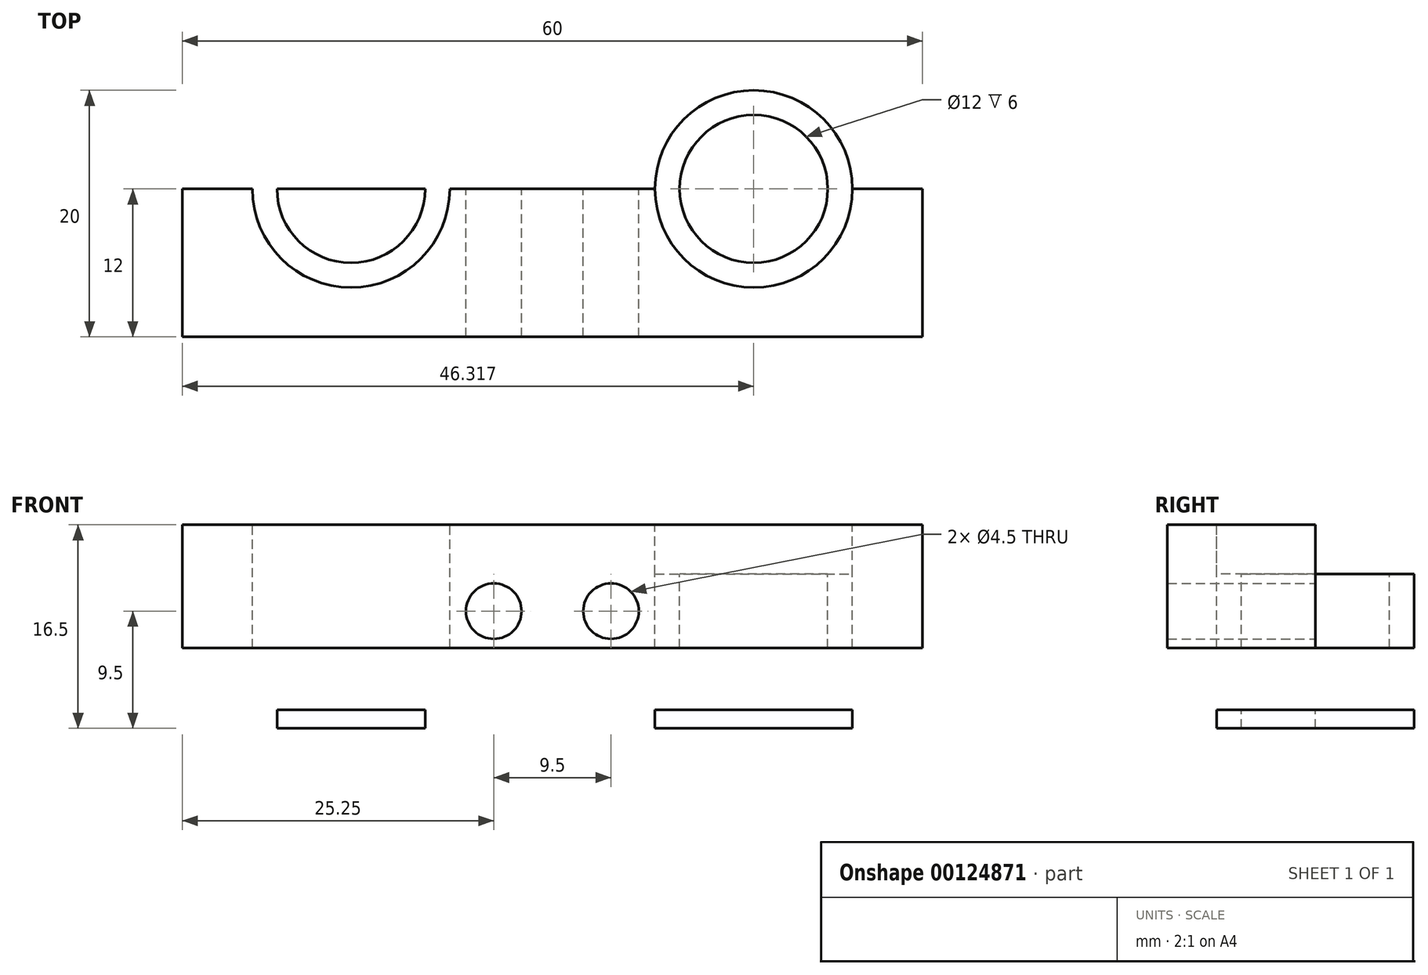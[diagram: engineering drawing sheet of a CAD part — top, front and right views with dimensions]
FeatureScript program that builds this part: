
annotation { "Feature Type Name" : "Feature", "Feature Type Description" : "" }
export const myFeature = defineFeature(function(context is Context, id is Id, definition is map)
    precondition{}
    {
        {
            var Q0;
            Q0=qCreatedBy(makeId("Top.planeOp"),FACE);
            var sketch = newSketch(context, id + "F0", { "sketchPlane" : qUnion([Q0])});
            skLineSegment(sketch, "E0.bottom", {"start": v(43, -44.5) * mm, "end": v(-43, -44.5) * mm});
            skLineSegment(sketch, "E0.top", {"start": v(43, 44.5) * mm, "end": v(-43, 44.5) * mm});
            skLineSegment(sketch, "E0.left", {"start": v(43, -44.5) * mm, "end": v(43, 44.5) * mm});
            skLineSegment(sketch, "E0.right", {"start": v(-43, -44.5) * mm, "end": v(-43, 44.5) * mm});
            skPoint(sketch, "E0.middle", {"position": v(0, 0) * mm});
            skLineSegment(sketch, "E1.bottom", {"start": v(-31, 25.5) * mm, "end": v(31, 25.5) * mm});
            skLineSegment(sketch, "E1.top", {"start": v(-31, -11.5) * mm, "end": v(31, -11.5) * mm});
            skLineSegment(sketch, "E1.left", {"start": v(-31, 25.5) * mm, "end": v(-31, -11.5) * mm});
            skLineSegment(sketch, "E1.right", {"start": v(31, 25.5) * mm, "end": v(31, -11.5) * mm});
            skLineSegment(sketch, "E2.bottom", {"start": v(43, 13.5) * mm, "end": v(31, 13.5) * mm});
            skLineSegment(sketch, "E2.top", {"start": v(43, -3) * mm, "end": v(31, -3) * mm});
            skLineSegment(sketch, "E2.left", {"start": v(43, 13.5) * mm, "end": v(43, -3) * mm});
            skLineSegment(sketch, "E2.right", {"start": v(-43, 13.5) * mm, "end": v(-43, -3) * mm});
            skLineSegment(sketch, "E3", {"start": v(-43, 5.25) * mm, "end": v(-31, 5.25) * mm, "construction": true});
            skLineSegment(sketch, "E4.trimOffspring", {"start": v(-31, 13.5) * mm, "end": v(-43, 13.5) * mm});
            skLineSegment(sketch, "E5.trimOffspring", {"start": v(-31, -3) * mm, "end": v(-43, -3) * mm});
            skLineSegment(sketch, "E6.trimOffspring", {"start": v(31, 5.25) * mm, "end": v(43, 5.25) * mm, "construction": true});
            skPoint(sketch, "E7", {"position": v(-37, 5.25) * mm});
            skPoint(sketch, "E8", {"position": v(37, 5.25) * mm});
            skCircle(sketch, "E9", {"center": v(37, 5.25) * mm, "radius": 1.6 * mm});
            skPoint(sketch, "E10", {"position": v(38.6, 5.25) * mm});
            skCircle(sketch, "E11.MirrorC", {"center": v(-37, 5.25) * mm, "radius": 1.6 * mm});
            skSolve(sketch);
        }
        {
            var Q0;
            Q0=qSketchRegion(id+"F0",true);
            extrude(context, id + "F1", {"entities" : qUnion([Q0]), "depth" : 17.5 * mm});
        }
        {
            var Q0;
            Q0=makeQuery(id+"F1.opExtrude","CAP_FACE",FACE,{"disambiguationData":[OSD([sQuery(id+"F0.wireOp",EDGE,"E0.bottom"),sQuery(id+"F0.wireOp",EDGE,"E0.top"),sQuery(id+"F0.wireOp",EDGE,"E0.left"),sQuery(id+"F0.wireOp",EDGE,"E0.right"),sQuery(id+"F0.wireOp",EDGE,"E1.bottom"),sQuery(id+"F0.wireOp",EDGE,"E1.top"),sQuery(id+"F0.wireOp",EDGE,"E1.left"),sQuery(id+"F0.wireOp",EDGE,"E1.right"),sQuery(id+"F0.wireOp",EDGE,"E2.left"),sQuery(id+"F0.wireOp",EDGE,"E2.right"),sQuery(id+"F0.wireOp",EDGE,"E9"),sQuery(id+"F0.wireOp",EDGE,"E11.MirrorC")])],"isStart":false});
            var sketch = newSketch(context, id + "F2", { "sketchPlane" : qUnion([Q0])});
            skLineSegment(sketch, "E12.bottom", {"start": v(43, -2.95) * mm, "end": v(31, -2.95) * mm});
            skLineSegment(sketch, "E12.top", {"start": v(43, 13.45) * mm, "end": v(31, 13.45) * mm});
            skLineSegment(sketch, "E12.left", {"start": v(43, -2.95) * mm, "end": v(43, 13.45) * mm});
            skLineSegment(sketch, "E12.right", {"start": v(-43, -2.95) * mm, "end": v(-43, 13.45) * mm});
            skPoint(sketch, "E13", {"position": v(37, 5.25) * mm});
            skLineSegment(sketch, "E14", {"start": v(43, 5.25) * mm, "end": v(31, 5.25) * mm, "construction": true});
            skLineSegment(sketch, "E15.0", {"start": v(31, 25.5) * mm, "end": v(31, -11.5) * mm});
            skLineSegment(sketch, "E15.1", {"start": v(-31, 25.5) * mm, "end": v(-31, -11.5) * mm});
            skLineSegment(sketch, "E16.trimOffspring", {"start": v(-31, -2.95) * mm, "end": v(-43, -2.95) * mm});
            skLineSegment(sketch, "E17.trimOffspring", {"start": v(-31, 13.45) * mm, "end": v(-43, 13.45) * mm});
            skLineSegment(sketch, "E18.trimOffspring", {"start": v(-31, 5.25) * mm, "end": v(-43, 5.25) * mm, "construction": true});
            skSolve(sketch);
        }
        {
            var Q0;
            Q0=qCreatedBy(makeId("Top.planeOp"),FACE);
            var sketch = newSketch(context, id + "F3", { "sketchPlane" : qUnion([Q0])});
            skCircle(sketch, "E19", {"center": v(16.32, 5.25) * mm, "radius": 11.2 * mm});
            skCircle(sketch, "E20.0", {"center": v(-37, 5.25) * mm, "radius": 1.6 * mm});
            skLineSegment(sketch, "E21", {"start": v(-37, 5.25) * mm, "end": v(47.23, 5.25) * mm, "construction": true});
            skCircle(sketch, "E22.MirrorC", {"center": v(-16.32, 5.25) * mm, "radius": 11.2 * mm});
            skSolve(sketch);
        }
        {
            var Q0;
            Q0=makeQuery(id+"F3.imprint","IMPRINT",FACE,{"disambiguationData":[TD([[makeQuery(id+"F3.imprint","IMPRINT",EDGE,{"derivedFrom":sQuery(id+"F3.wireOp",EDGE,"E19")}),1.0]])]});
            var Q1;
            Q1=makeQuery(id+"F3.imprint","IMPRINT",FACE,{"disambiguationData":[TD([[makeQuery(id+"F3.imprint","IMPRINT",EDGE,{"derivedFrom":sQuery(id+"F3.wireOp",EDGE,"E22.MirrorC")}),-1.0]])]});
            extrude(context, id + "F4", {"entities" : qUnion([Q0, Q1]), "depth" : (26 + 14.5) * mm, "hasSecondDirection" : true, "secondDirectionOppositeDirection" : false, "secondDirectionDepth" : 14.5 * mm});
        }
        {
            var Q0;
            Q0=makeQuery(id+"F1.opExtrude","CAP_FACE",FACE,{"disambiguationData":[OSD([sQuery(id+"F0.wireOp",EDGE,"E0.bottom"),sQuery(id+"F0.wireOp",EDGE,"E0.top"),sQuery(id+"F0.wireOp",EDGE,"E0.left"),sQuery(id+"F0.wireOp",EDGE,"E0.right"),sQuery(id+"F0.wireOp",EDGE,"E1.bottom"),sQuery(id+"F0.wireOp",EDGE,"E1.top"),sQuery(id+"F0.wireOp",EDGE,"E1.left"),sQuery(id+"F0.wireOp",EDGE,"E1.right"),sQuery(id+"F0.wireOp",EDGE,"E2.left"),sQuery(id+"F0.wireOp",EDGE,"E2.right"),sQuery(id+"F0.wireOp",EDGE,"E9"),sQuery(id+"F0.wireOp",EDGE,"E11.MirrorC")])],"isStart":false});
            var sketch = newSketch(context, id + "F5", { "sketchPlane" : qUnion([Q0])});
            skLineSegment(sketch, "E23.bottom", {"start": v(-43, 13.5) * mm, "end": v(-31, 13.5) * mm});
            skLineSegment(sketch, "E23.top", {"start": v(-43, -3) * mm, "end": v(-31, -3) * mm});
            skLineSegment(sketch, "E23.left", {"start": v(-43, 13.5) * mm, "end": v(-43, -3) * mm});
            skLineSegment(sketch, "E23.right", {"start": v(43, 13.5) * mm, "end": v(43, -3) * mm});
            skPoint(sketch, "E24", {"position": v(43, 5.25) * mm});
            skPoint(sketch, "E25", {"position": v(-43, 5.25) * mm});
            skLineSegment(sketch, "E26", {"start": v(-31, 13.5) * mm, "end": v(-31, -3) * mm});
            skLineSegment(sketch, "E27", {"start": v(31, 13.5) * mm, "end": v(31, -3) * mm});
            skLineSegment(sketch, "E28.trimOffspring", {"start": v(31, 13.5) * mm, "end": v(43, 13.5) * mm});
            skLineSegment(sketch, "E29.trimOffspring", {"start": v(31, -3) * mm, "end": v(43, -3) * mm});
            skSolve(sketch);
        }
        {
            var Q0;
            Q0=qSketchRegion(id+"F5",true);
            extrude(context, id + "F6", {"entities" : qUnion([Q0]), "operationType" : NewBodyOperationType.REMOVE, "oppositeDirection" : true, "depth" : 3 * mm});
        }
        {
            var Q0;
            Q0=qSketchRegion(id+"F2",true);
            extrude(context, id + "F7", {"entities" : qUnion([Q0]), "depth" : 39.5 * mm, "hasSecondDirection" : true, "secondDirectionOppositeDirection" : true, "secondDirectionDepth" : 3 * mm});
        }
        {
            var Q0;
            Q0=makeQuery(id+"F4.opExtrude","CAP_FACE",FACE,{"disambiguationData":[OSD([sQuery(id+"F3.wireOp",EDGE,"E19")])],"isStart":false});
            cPlane(context, id + "F8", {"entities" : qUnion([Q0]), "cplaneType" : CPlaneType.OFFSET, "offset" : 0 * mm, "width" : 150 * mm, "height" : 150 * mm});
        }
        {
            var Q0;
            Q0=qCreatedBy(id+"F8.planeOp",FACE);
            var sketch = newSketch(context, id + "F9", { "sketchPlane" : qUnion([Q0])});
            skCircle(sketch, "E30", {"center": v(16.32, 5.25) * mm, "radius": 8 * mm});
            skCircle(sketch, "E31.MirrorC", {"center": v(-16.32, 5.25) * mm, "radius": 8 * mm});
            skSolve(sketch);
        }
        {
            var Q0;
            Q0=qSketchRegion(id+"F9",true);
            extrude(context, id + "F10", {"entities" : qUnion([Q0]), "depth" : 16.5 * mm});
        }
        {
            var Q0;
            Q0=makeQuery(id+"F1.opExtrude","SWEPT_FACE",FACE,{"disambiguationData":[OSD([sQuery(id+"F0.wireOp",EDGE,"E0.right"),sQuery(id+"F0.wireOp",EDGE,"E2.right")])]});
            var sketch = newSketch(context, id + "F11", { "sketchPlane" : qUnion([Q0])});
            skLineSegment(sketch, "E32.bottom", {"start": v(-25, 0) * mm, "end": v(25, 0) * mm});
            skLineSegment(sketch, "E32.top", {"start": v(-25, 5.5) * mm, "end": v(25, 5.5) * mm});
            skLineSegment(sketch, "E32.left", {"start": v(-25, 0) * mm, "end": v(-25, 5.5) * mm});
            skLineSegment(sketch, "E32.right", {"start": v(25, 0) * mm, "end": v(25, 5.5) * mm});
            skSolve(sketch);
        }
        {
            var Q0;
            Q0=qSketchRegion(id+"F11",true);
            extrude(context, id + "F12", {"entities" : qUnion([Q0]), "operationType" : NewBodyOperationType.REMOVE, "oppositeDirection" : true, "depth" : 90 * mm});
        }
        {
            var Q0;
            Q0=makeQuery(id+"F7.opExtrude","CAP_FACE",FACE,{"disambiguationData":[OSD([sQuery(id+"F2.wireOp",EDGE,"E12.right"),sQuery(id+"F2.wireOp",EDGE,"E15.1"),sQuery(id+"F2.wireOp",EDGE,"E16.trimOffspring"),sQuery(id+"F2.wireOp",EDGE,"E17.trimOffspring")])],"isStart":false});
            var sketch = newSketch(context, id + "F13", { "sketchPlane" : qUnion([Q0])});
            skLineSegment(sketch, "E33.0", {"start": v(43, 13.5) * mm, "end": v(43, 17.25) * mm});
            skLineSegment(sketch, "E34.bottom", {"start": v(-43, -6.75) * mm, "end": v(43, -6.75) * mm});
            skLineSegment(sketch, "E34.top", {"start": v(-43, 17.25) * mm, "end": v(43, 17.25) * mm});
            skLineSegment(sketch, "E34.left", {"start": v(-43, -6.75) * mm, "end": v(-43, 17.25) * mm});
            skLineSegment(sketch, "E34.right", {"start": v(43, -6.75) * mm, "end": v(43, 17.25) * mm});
            skSolve(sketch);
        }
        {
            var Q0;
            Q0=qSketchRegion(id+"F13",true);
            extrude(context, id + "F14", {"entities" : qUnion([Q0]), "operationType" : NewBodyOperationType.ADD, "oppositeDirection" : true, "depth" : 10 * mm});
        }
        {
            var Q0;
            Q0=makeQuery(id+"F7.opExtrude","CAP_FACE",FACE,{"disambiguationData":[OSD([sQuery(id+"F2.wireOp",EDGE,"E12.bottom"),sQuery(id+"F2.wireOp",EDGE,"E12.top"),sQuery(id+"F2.wireOp",EDGE,"E12.left"),sQuery(id+"F2.wireOp",EDGE,"E15.0")])],"isStart":true});
            var sketch = newSketch(context, id + "F15", { "sketchPlane" : qUnion([Q0])});
            skCircle(sketch, "E35.0", {"center": v(37, -5.25) * mm, "radius": 1.6 * mm});
            skCircle(sketch, "E35.1", {"center": v(-37, -5.25) * mm, "radius": 1.6 * mm});
            skSolve(sketch);
        }
        {
            var Q0;
            Q0=qSketchRegion(id+"F15",true);
            extrude(context, id + "F16", {"entities" : qUnion([Q0]), "operationType" : NewBodyOperationType.REMOVE, "oppositeDirection" : true, "depth" : 7 * mm});
        }
        {
            var Q0;
            Q0=makeQuery(id+"F14.boolean.opBoolean","MERGE",FACE,{"derivedFrom":[makeQuery(id+"F7.opExtrude","CAP_FACE",FACE,{"disambiguationData":[OSD([sQuery(id+"F2.wireOp",EDGE,"E12.bottom"),sQuery(id+"F2.wireOp",EDGE,"E12.top"),sQuery(id+"F2.wireOp",EDGE,"E12.left"),sQuery(id+"F2.wireOp",EDGE,"E15.0")])],"isStart":false}),makeQuery(id+"F7.opExtrude","CAP_FACE",FACE,{"disambiguationData":[OSD([sQuery(id+"F2.wireOp",EDGE,"E12.right"),sQuery(id+"F2.wireOp",EDGE,"E15.1"),sQuery(id+"F2.wireOp",EDGE,"E16.trimOffspring"),sQuery(id+"F2.wireOp",EDGE,"E17.trimOffspring")])],"isStart":false}),makeQuery(id+"F14.opExtrude","CAP_FACE",FACE,{"disambiguationData":[OSD([sQuery(id+"F13.wireOp",EDGE,"E34.bottom"),sQuery(id+"F13.wireOp",EDGE,"E34.top"),sQuery(id+"F13.wireOp",EDGE,"E34.left"),sQuery(id+"F13.wireOp",EDGE,"E34.right")])],"isStart":true})]});
            var sketch = newSketch(context, id + "F17", { "sketchPlane" : qUnion([Q0])});
            skCircle(sketch, "E36.0", {"center": v(16.32, 5.25) * mm, "radius": 8 * mm});
            skCircle(sketch, "E36.1", {"center": v(-16.32, 5.25) * mm, "radius": 8 * mm});
            skSolve(sketch);
        }
        {
            var Q0;
            Q0=qSketchRegion(id+"F17",true);
            extrude(context, id + "F18", {"entities" : qUnion([Q0]), "operationType" : NewBodyOperationType.REMOVE, "oppositeDirection" : true, "depth" : 15 * mm});
        }
        {
            var Q0;
            Q0=makeQuery(id+"F1.opExtrude","SWEPT_BODY",BODY,{"disambiguationData":[OSD([sQuery(id+"F0.wireOp",EDGE,"E0.bottom"),sQuery(id+"F0.wireOp",EDGE,"E0.top"),sQuery(id+"F0.wireOp",EDGE,"E0.left"),sQuery(id+"F0.wireOp",EDGE,"E0.right"),sQuery(id+"F0.wireOp",EDGE,"E1.bottom"),sQuery(id+"F0.wireOp",EDGE,"E1.top"),sQuery(id+"F0.wireOp",EDGE,"E1.left"),sQuery(id+"F0.wireOp",EDGE,"E1.right"),sQuery(id+"F0.wireOp",EDGE,"E2.left"),sQuery(id+"F0.wireOp",EDGE,"E2.right"),sQuery(id+"F0.wireOp",EDGE,"E9"),sQuery(id+"F0.wireOp",EDGE,"E11.MirrorC")])]});
            deleteBodies(context, id + "F19", {"entities" : qUnion([Q0])});
        }
        {
            var Q0;
            Q0=makeQuery(id+"F4.opExtrude","SWEPT_BODY",BODY,{"disambiguationData":[OSD([sQuery(id+"F3.wireOp",EDGE,"E19")])]});
            var Q1;
            Q1=makeQuery(id+"F4.opExtrude","SWEPT_BODY",BODY,{"disambiguationData":[OSD([sQuery(id+"F3.wireOp",EDGE,"E22.MirrorC")])]});
            var Q2;
            Q2=makeQuery(id+"F10.opExtrude","SWEPT_BODY",BODY,{"disambiguationData":[OSD([sQuery(id+"F9.wireOp",EDGE,"E30")])]});
            var Q3;
            Q3=makeQuery(id+"F10.opExtrude","SWEPT_BODY",BODY,{"disambiguationData":[OSD([sQuery(id+"F9.wireOp",EDGE,"E31.MirrorC")])]});
            deleteBodies(context, id + "F20", {"entities" : qUnion([Q0, Q1, Q2, Q3])});
        }
        {
            var Q0;
            Q0=makeQuery(id+"F14.boolean.opBoolean","MERGE",FACE,{"derivedFrom":[makeQuery(id+"F7.opExtrude","CAP_FACE",FACE,{"disambiguationData":[OSD([sQuery(id+"F2.wireOp",EDGE,"E12.bottom"),sQuery(id+"F2.wireOp",EDGE,"E12.top"),sQuery(id+"F2.wireOp",EDGE,"E12.left"),sQuery(id+"F2.wireOp",EDGE,"E15.0")])],"isStart":false}),makeQuery(id+"F7.opExtrude","CAP_FACE",FACE,{"disambiguationData":[OSD([sQuery(id+"F2.wireOp",EDGE,"E12.right"),sQuery(id+"F2.wireOp",EDGE,"E15.1"),sQuery(id+"F2.wireOp",EDGE,"E16.trimOffspring"),sQuery(id+"F2.wireOp",EDGE,"E17.trimOffspring")])],"isStart":false}),makeQuery(id+"F14.opExtrude","CAP_FACE",FACE,{"disambiguationData":[OSD([sQuery(id+"F13.wireOp",EDGE,"E34.bottom"),sQuery(id+"F13.wireOp",EDGE,"E34.top"),sQuery(id+"F13.wireOp",EDGE,"E34.left"),sQuery(id+"F13.wireOp",EDGE,"E34.right")])],"isStart":true})]});
            cPlane(context, id + "F21", {"entities" : qUnion([Q0]), "cplaneType" : CPlaneType.OFFSET, "offset" : 4 * mm, "oppositeDirection" : true, "width" : 150 * mm, "height" : 150 * mm});
        }
        {
            var Q0;
            Q0=qCreatedBy(id+"F21.planeOp",FACE);
            var sketch = newSketch(context, id + "F22", { "sketchPlane" : qUnion([Q0])});
            skCircle(sketch, "E37.0", {"center": v(-16.32, 5.25) * mm, "radius": 8 * mm});
            skCircle(sketch, "E38", {"center": v(-16.32, 5.25) * mm, "radius": 6 * mm});
            skCircle(sketch, "E39.MirrorC", {"center": v(16.32, 5.25) * mm, "radius": 6 * mm});
            skCircle(sketch, "E40.0", {"center": v(16.32, 5.25) * mm, "radius": 8 * mm});
            skSolve(sketch);
        }
        {
            var Q0;
            Q0=qSketchRegion(id+"F22",true);
            extrude(context, id + "F23", {"entities" : qUnion([Q0]), "operationType" : NewBodyOperationType.ADD, "oppositeDirection" : true, "depth" : 6 * mm});
        }
        {
            var Q0;
            Q0=makeQuery(id+"F14.boolean.opBoolean","MERGE",FACE,{"derivedFrom":[makeQuery(id+"F7.opExtrude","CAP_FACE",FACE,{"disambiguationData":[OSD([sQuery(id+"F2.wireOp",EDGE,"E12.bottom"),sQuery(id+"F2.wireOp",EDGE,"E12.top"),sQuery(id+"F2.wireOp",EDGE,"E12.left"),sQuery(id+"F2.wireOp",EDGE,"E15.0")])],"isStart":false}),makeQuery(id+"F7.opExtrude","CAP_FACE",FACE,{"disambiguationData":[OSD([sQuery(id+"F2.wireOp",EDGE,"E12.right"),sQuery(id+"F2.wireOp",EDGE,"E15.1"),sQuery(id+"F2.wireOp",EDGE,"E16.trimOffspring"),sQuery(id+"F2.wireOp",EDGE,"E17.trimOffspring")])],"isStart":false}),makeQuery(id+"F14.opExtrude","CAP_FACE",FACE,{"disambiguationData":[OSD([sQuery(id+"F13.wireOp",EDGE,"E34.bottom"),sQuery(id+"F13.wireOp",EDGE,"E34.top"),sQuery(id+"F13.wireOp",EDGE,"E34.left"),sQuery(id+"F13.wireOp",EDGE,"E34.right")])],"isStart":true})]});
            var sketch = newSketch(context, id + "F24", { "sketchPlane" : qUnion([Q0])});
            skLineSegment(sketch, "E41.bottom", {"start": v(-30, -6.75) * mm, "end": v(30, -6.75) * mm});
            skLineSegment(sketch, "E41.top", {"start": v(-30, 5.25) * mm, "end": v(30, 5.25) * mm});
            skLineSegment(sketch, "E41.left", {"start": v(-30, -6.75) * mm, "end": v(-30, 5.25) * mm});
            skLineSegment(sketch, "E41.right", {"start": v(30, -6.75) * mm, "end": v(30, 5.25) * mm});
            skCircle(sketch, "E42.0", {"center": v(-16.32, 5.25) * mm, "radius": 6 * mm});
            skSolve(sketch);
        }
        {
            var Q0;
            {var subQ0=sQuery(id+"F24.wireOp",EDGE,"E42.0");var subQ1=sQuery(id+"F24.wireOp",EDGE,"E41.top");var subQ2=makeQuery(id+"F24.imprint","INTERSECT",VERTEX,{"disambiguationData":[OD(0.0)],"derivedFrom":[subQ1,subQ0]});Q0=makeQuery(id+"F24.imprint","IMPRINT",FACE,{"disambiguationData":[TD([[makeQuery(id+"F24.imprint","IMPRINT",EDGE,{"disambiguationData":[TD([[subQ2,-1.0]])],"derivedFrom":subQ1}),1.0]])]});}
            var Q1;
            {var subQ0=sQuery(id+"F24.wireOp",EDGE,"E42.0");var subQ1=sQuery(id+"F24.wireOp",EDGE,"E41.top");var subQ2=makeQuery(id+"F24.imprint","INTERSECT",VERTEX,{"disambiguationData":[OD(0.0)],"derivedFrom":[subQ1,subQ0]});Q1=makeQuery(id+"F24.imprint","IMPRINT",FACE,{"disambiguationData":[TD([[makeQuery(id+"F24.imprint","IMPRINT",EDGE,{"disambiguationData":[TD([[subQ2,-1.0]])],"derivedFrom":subQ1}),-1.0]])]});}
            var Q2;
            {var subQ3=sQuery(id+"F24.wireOp",EDGE,"E41.left");Q2=makeQuery(id+"F24.imprint","IMPRINT",FACE,{"disambiguationData":[TD([[makeQuery(id+"F24.imprint","IMPRINT",EDGE,{"derivedFrom":subQ3}),1.0]])]});}
            var Q3;
            {var subQ0=sQuery(id+"F24.wireOp",EDGE,"E42.0");var subQ1=sQuery(id+"F24.wireOp",EDGE,"E41.top");var subQ2=makeQuery(id+"F24.imprint","INTERSECT",VERTEX,{"disambiguationData":[OD(0.0)],"derivedFrom":[subQ1,subQ0]});Q3=makeQuery(id+"F24.imprint","IMPRINT",FACE,{"disambiguationData":[TD([[makeQuery(id+"F24.imprint","IMPRINT",EDGE,{"disambiguationData":[TD([[subQ2,1.0]])],"derivedFrom":subQ1}),1.0]])]});}
            var Q4;
            {var subQ0=sQuery(id+"F24.wireOp",EDGE,"E41.top");var subQ1=makeQuery(id+"F18.boolean.opBoolean","COPY",EDGE,{"derivedFrom":makeQuery(id+"F18.opExtrude","CAP_EDGE",EDGE,{"disambiguationData":[OSD([sQuery(id+"F17.wireOp",EDGE,"E36.0")])],"isStart":true})});var subQ2=makeQuery(id+"F24.imprint","INTERSECT",VERTEX,{"disambiguationData":[OD(0.0)],"derivedFrom":[subQ1,subQ0]});Q4=makeQuery(id+"F24.imprint","IMPRINT",FACE,{"disambiguationData":[TD([[makeQuery(id+"F24.imprint","IMPRINT",EDGE,{"disambiguationData":[TD([[subQ2,-1.0]])],"derivedFrom":subQ0}),1.0]])]});}
            extrude(context, id + "F25", {"entities" : qUnion([Q0, Q1, Q2, Q3, Q4]), "operationType" : NewBodyOperationType.REMOVE, "endBound" : BoundingType.THROUGH_ALL, "oppositeDirection" : true, "depth" : 25 * mm});
        }
        {
            var Q0;
            {var subQ5=sQuery(id+"F17.wireOp",EDGE,"E36.0");var subQ8=sQuery(id+"F17.wireOp",EDGE,"E36.1");var subQ10=sQuery(id+"F24.wireOp",EDGE,"E41.top");var subQ11=makeQuery(id+"F18.boolean.opBoolean","COPY",EDGE,{"derivedFrom":makeQuery(id+"F18.opExtrude","CAP_EDGE",EDGE,{"disambiguationData":[OSD([subQ5])],"isStart":true})});var subQ13=makeQuery(id+"F24.imprint","INTERSECT",VERTEX,{"disambiguationData":[OD(0.0)],"derivedFrom":[subQ11,subQ10]});var subQ14=makeQuery(id+"F24.imprint","INTERSECT",VERTEX,{"disambiguationData":[OD(1.0)],"derivedFrom":[makeQuery(id+"F18.boolean.opBoolean","COPY",EDGE,{"derivedFrom":makeQuery(id+"F18.opExtrude","CAP_EDGE",EDGE,{"disambiguationData":[OSD([subQ8])],"isStart":true})}),subQ10]});Q0=makeQuery(id+"F25.boolean.opBoolean","COPY",FACE,{"disambiguationData":[TD([makeQuery(id+"F18.boolean.opBoolean","COPY",FACE,{"derivedFrom":makeQuery(id+"F18.opExtrude","SWEPT_FACE",FACE,{"disambiguationData":[OSD([subQ8])]})})])],"derivedFrom":makeQuery(id+"F25.opExtrude","SWEPT_FACE",FACE,{"disambiguationData":[OSD([subQ10]),TDD([makeQuery(id+"F24.imprint","IMPRINT",EDGE,{"disambiguationData":[TD([[makeQuery(id+"F24.imprint","INTERSECT",VERTEX,{"disambiguationData":[OD(1.0)],"derivedFrom":[subQ10,sQuery(id+"F24.wireOp",EDGE,"E42.0")]}),-1.0]])],"derivedFrom":subQ10}),makeQuery(id+"F24.imprint","IMPRINT",EDGE,{"disambiguationData":[TD([[subQ14,-1.0]])],"derivedFrom":subQ10}),makeQuery(id+"F24.imprint","IMPRINT",EDGE,{"disambiguationData":[TD([[subQ13,-1.0]])],"derivedFrom":subQ10}),makeQuery(id+"F24.imprint","IMPRINT",EDGE,{"disambiguationData":[TD([[makeQuery(id+"F24.imprint","INTERSECT",VERTEX,{"derivedFrom":[subQ10,sQuery(id+"F24.wireOp",EDGE,"E41.right")]}),1.0]])],"derivedFrom":subQ10})])]})});}
            var sketch = newSketch(context, id + "F26", { "sketchPlane" : qUnion([Q0])});
            skLineSegment(sketch, "E43.0", {"start": v(-10.32, 53) * mm, "end": v(-10.32, 47) * mm});
            skLineSegment(sketch, "E44", {"start": v(-10.32, 50) * mm, "end": v(10.32, 50) * mm, "construction": true});
            skPoint(sketch, "E45", {"position": v(-4.75, 50) * mm});
            skCircle(sketch, "E46", {"center": v(-4.75, 50) * mm, "radius": 2.25 * mm});
            skCircle(sketch, "E47.MirrorC", {"center": v(4.75, 50) * mm, "radius": 2.25 * mm});
            skSolve(sketch);
        }
        {
            var Q0;
            Q0 = qSketchRegion(id + "F26", true);
            extrude(context, id + "F27", {"entities" : qUnion([Q0]), "operationType" : NewBodyOperationType.REMOVE, "oppositeDirection" : true, "depth" : 25 * mm});
        }
    });
